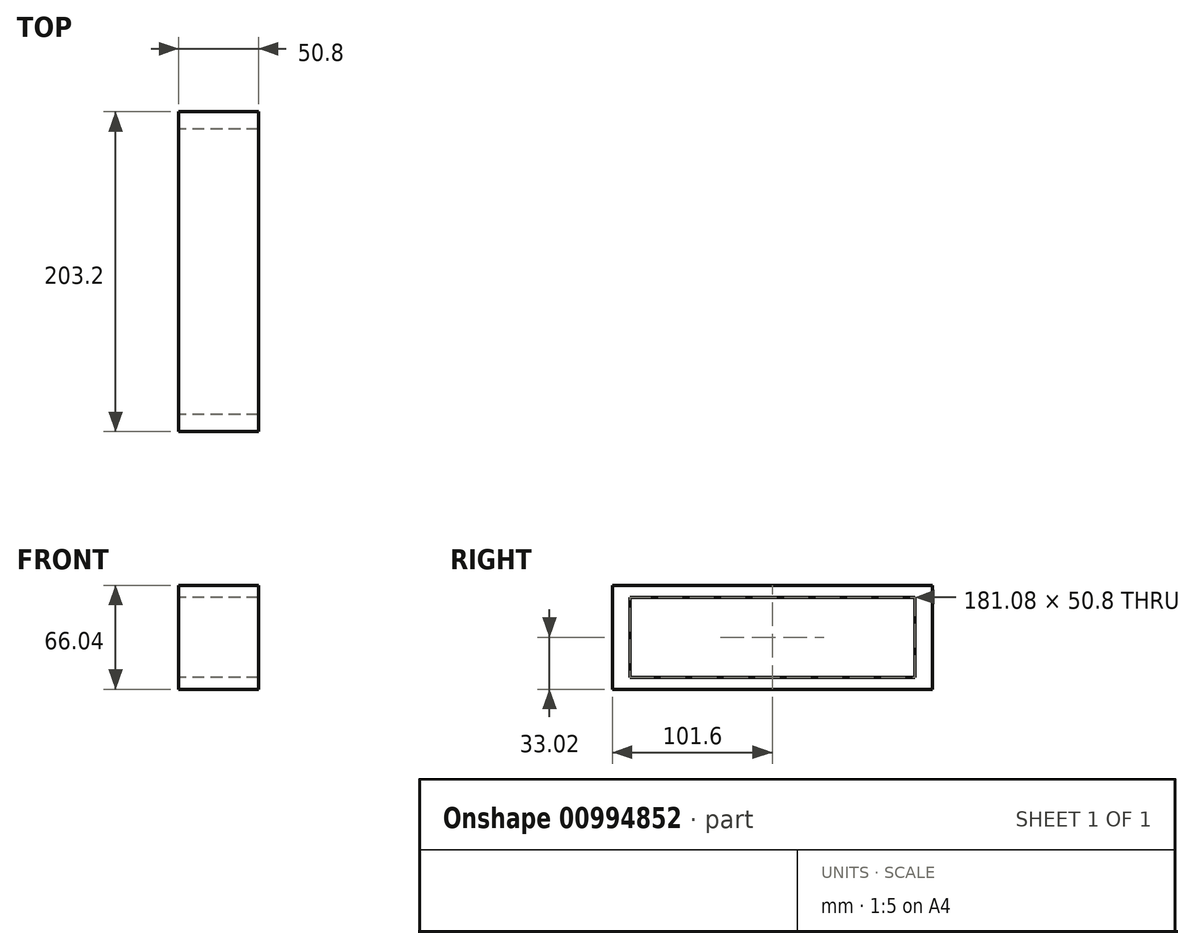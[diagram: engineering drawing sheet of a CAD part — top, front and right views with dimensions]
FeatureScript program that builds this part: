
annotation { "Feature Type Name" : "Feature", "Feature Type Description" : "" }
export const myFeature = defineFeature(function(context is Context, id is Id, definition is map)
    precondition{}
    {
        {
            var Q0;
            Q0=qCreatedBy(makeId("Right.planeOp"),FACE);
            var sketch = newSketch(context, id + "F0", { "sketchPlane" : qUnion([Q0])});
            skLineSegment(sketch, "E0.bottom", {"start": v(101.6, -33.02) * mm, "end": v(-101.6, -33.02) * mm});
            skLineSegment(sketch, "E0.top", {"start": v(101.6, 33.02) * mm, "end": v(-101.6, 33.02) * mm});
            skLineSegment(sketch, "E0.left", {"start": v(101.6, -33.02) * mm, "end": v(101.6, 33.02) * mm});
            skLineSegment(sketch, "E0.right", {"start": v(-101.6, -33.02) * mm, "end": v(-101.6, 33.02) * mm});
            skPoint(sketch, "E0.middle", {"position": v(0, 0) * mm});
            skLineSegment(sketch, "E1.bottom", {"start": v(-90.54, 25.4) * mm, "end": v(90.54, 25.4) * mm});
            skLineSegment(sketch, "E1.top", {"start": v(-90.54, -25.4) * mm, "end": v(90.54, -25.4) * mm});
            skLineSegment(sketch, "E1.left", {"start": v(-90.54, 25.4) * mm, "end": v(-90.54, -25.4) * mm});
            skLineSegment(sketch, "E1.right", {"start": v(90.54, 25.4) * mm, "end": v(90.54, -25.4) * mm});
            skSolve(sketch);
        }
        {
            var Q0;
            Q0=makeQuery(id+"F0.imprint","IMPRINT",FACE,{"disambiguationData":[TD([[makeQuery(id+"F0.imprint","IMPRINT",EDGE,{"derivedFrom":sQuery(id+"F0.wireOp",EDGE,"E0.bottom")}),-1.0]])]});
            extrude(context, id + "F1", {"entities" : qUnion([Q0]), "depth" : 50.8 * mm, "offsetDistance" : 25.4 * mm});
        }
    });
